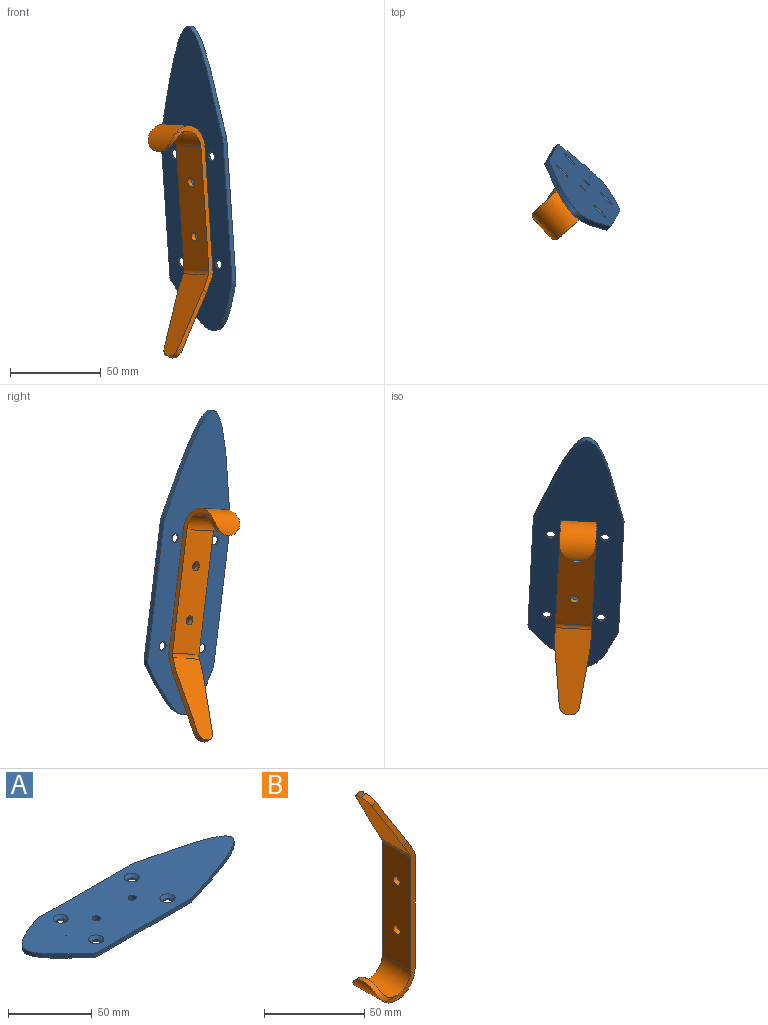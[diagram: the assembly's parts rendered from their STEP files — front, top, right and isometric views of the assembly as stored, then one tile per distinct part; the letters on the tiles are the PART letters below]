
ASSEMBLY  parts=2 mates=1
PART A: 22 faces, bbox 173.5x50x3 mm
  f0: extruded ~3x0.61mm, area 1.8mm2, adj f5,f6,f7
  f1: extruded ~61.02x49.65mm, area 404.2mm2, adj f6,f7,f8,f11
  f2: plane 78.56x3mm, normal (0,1,0), area 235.7mm2, adj f6,f7,f8,f9
  f3: extruded ~48.48x26.36mm, area 223mm2, adj f6,f7,f9,f10
  f4: plane 77.38x3mm, normal (0,-1,0), area 232.1mm2, adj f6,f7,f10,f11
  f5: plane 3x0.61mm, normal (1,0,0), area 1.8mm2, adj f0,f6,f7
  f6: plane 173.46x50mm, normal (0,0,1), area 6480.4mm2, adj f0,f1,f2,f3,f4,f5,f8,f9
  f7: plane 173.46x50mm, normal (0,0,-1), area 6656.3mm2, adj f0,f1,f2,f3,f4,f5,f8,f9
  f8: cylinder r=5mm len=3mm, axis (0,0,-1), area 3.4mm2, adj f1,f2,f6,f7
  f9: cylinder r=5mm len=3mm, axis (0,0,-1), area 5.2mm2, adj f2,f3,f6,f7
  f10: cylinder r=5mm len=3.28mm, axis (0,0,-1), area 10.7mm2, adj f3,f4,f6,f7
  f11: cylinder r=5mm len=3mm, axis (0,0,-1), area 4.5mm2, adj f1,f4,f6,f7
  f12: cylinder r=2.5mm len=5mm, axis (0,0,1), area 15.7mm2, adj f7,f19
  f13: cylinder r=2.5mm len=5mm, axis (0,0,1), area 15.7mm2, adj f7,f16
  f14: cylinder r=2.5mm len=5mm, axis (0,0,1), area 15.7mm2, adj f7,f17
  f15: cylinder r=2.5mm len=5mm, axis (0,0,1), area 15.7mm2, adj f7,f18
  f16: cone r=2.5mm half-angle=45deg, axis (0,0,1), area 62.2mm2, adj f6,f13
  f17: cone r=2.5mm half-angle=45deg, axis (0,0,1), area 62.2mm2, adj f6,f14
  f18: cone r=2.5mm half-angle=45deg, axis (0,0,1), area 62.2mm2, adj f6,f15
  f19: cone r=2.5mm half-angle=45deg, axis (0,0,1), area 62.2mm2, adj f6,f12
  f20: cylinder r=2.5mm len=5mm, axis (0,0,1), area 47.1mm2, adj f6,f7
  f21: cylinder r=2.5mm len=5mm, axis (0,0,1), area 47.1mm2, adj f6,f7
PART B: 18 faces, bbox 28x20x127.8 mm
  f0: cylinder r=13mm len=26mm, axis (0,1,0), area 772.6mm2, adj f1,f7,f8,f9
  f1: plane 69.46x20mm, normal (1,0,0), area 1350mm2, adj f0,f7,f8,f14,f15,f16
  f2: plane 42.84x24.73mm, normal (0.87,0,0.5), area 781.3mm2, adj f3,f7,f8,f10,f11,f12,f13,f16
  f3: plane 2.6x1.5mm, normal (-0.5,0,0.87), area 3.5mm2, adj f2,f4,f12,f13
  f4: plane 42.14x24.33mm, normal (-0.87,0,-0.5), area 765.2mm2, adj f3,f7,f8,f10,f11,f12,f13,f17
  f5: plane 68.66x20mm, normal (-1,0,0), area 1333.9mm2, adj f6,f7,f8,f14,f15,f17
  f6: cylinder r=10mm len=20mm, axis (0,1,0), area 582.9mm2, adj f5,f7,f8,f9
  f7: plane 93.16x21.31mm, normal (0,-1,0), area 313.6mm2, adj f0,f1,f2,f4,f5,f6,f9,f10
  f8: plane 93.16x21.31mm, normal (0,1,0), area 313.6mm2, adj f0,f1,f2,f4,f5,f6,f9,f11
  f9: cylinder r=10mm len=20mm, axis (1,0,0), area 109.2mm2, adj f0,f6,f7,f8
  f10: plane 32.35x20.41mm, normal (-0.06,-0.99,0.11), area 107.7mm2, adj f2,f4,f7,f12
  f11: plane 32.35x20.41mm, normal (-0.06,0.99,0.11), area 107.7mm2, adj f2,f4,f8,f13
  f12: cylinder r=5mm len=5.29mm, axis (-0.87,0,-0.5), area 21.7mm2, adj f2,f3,f4,f10
  f13: cylinder r=5mm len=5.29mm, axis (-0.87,0,-0.5), area 21.7mm2, adj f2,f3,f4,f11
  f14: cylinder r=2.5mm len=5mm, axis (-1,0,0), area 47.1mm2, adj f1,f5
  f15: cylinder r=2.5mm len=5mm, axis (-1,0,0), area 47.1mm2, adj f1,f5
  f16: cylinder r=5mm len=20mm, axis (0,1,0), area 52.4mm2, adj f1,f2,f7,f8
  f17: cylinder r=5mm len=20mm, axis (0,-1,0), area 52.4mm2, adj f4,f5,f7,f8
PLACE A rot(axis=(-0.65,-0.24,-0.72),146.5deg) t=(44.09,29.86,14.35)mm
PLACE B rot(axis=(-0.93,-0.37,-0.05),175.1deg) t=(58.93,-3.98,6.66)mm
MATE fastened B.f14 <-> A.f20  axis (0.73,0.67,0.13) through (62.83,14.4,-11.12)mm
